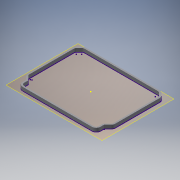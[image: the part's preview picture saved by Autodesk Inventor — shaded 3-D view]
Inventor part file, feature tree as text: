
AUTODESK INVENTOR PART (.ipt)
format: ipt  version: 2017 SP1 (Build 210196100, 196)  size: 916,992 bytes
history: native  units: mm
features: sketch x10, extrude x10, projected_geometry x7, fillet x4, reference x4, other x4, plane x3, shell x1
ambient origin geometry x8: Origin, YZ Plane, XZ Plane, XY Plane, X Axis, Y Axis, Z Axis, Center Point
bodies: Body1 (feature_tree)
feature tree (43):
  plane  "Arbeitsebene3"
  sketch  "Skizze2"  dims[d4=0.3mm d5=0.0mm d6=0.5mm d7=5.0mm d8=0.0mm]
  extrude  "Extrusion2"  Depth=0.5mm
  shell  "Wandung1"  Thickness=5.0mm
  sketch  "Skizze5"  dims[d14=5.0mm d15=0.0mm d18=0.5mm d19=0.0mm]
  plane  "Arbeitsebene4"
  extrude  "Extrusion3"  Depth=0.5mm TaperAngle=0.0deg
  extrude  "Extrusion4"  Depth=2.0mm
  extrude  "Extrusion6"  Depth=30.0mm
  extrude  "Extrusion7"  Depth=3.0mm
  fillet  "Rundung1"  Radius=3.0mm
  extrude  "Extrusion8"  Depth=2.0mm TaperAngle=0.0deg
  fillet  "Rundung2"  Radius=1.0mm
  extrude  "Extrusion9"  Depth=10.0mm
  fillet  "Rundung3"  Radius=3.0mm
  plane  "Arbeitsebene5"
  extrude  "Extrusion10"  Depth=1.0mm
  extrude  "Extrusion11"  Depth=11.0mm
  fillet  "Rundung4"  Radius=11.0mm
  extrude  "Extrusion12"  Depth=0.1mm
  reference  "Referenz1"
  sketch  "Skizze6"  dims[d20=3.0mm d21=0.0mm d22=2.0mm]
  projected_geometry  "Projizierte Kontur3"
  sketch  "Skizze8"  dims[d23=30.0mm d24=30.0mm]
  projected_geometry  "Projizierte Kontur5"
  sketch  "Skizze9"  dims[d25=3.0mm d26=3.0mm d27=3.0mm]
  projected_geometry  "Projizierte Kontur6"
  sketch  "Skizze11"  dims[d28=3.0mm d29=2.0mm d30=0.0mm d31=1.0mm]
  projected_geometry  "Projizierte Kontur7"
  sketch  "Skizze12"  dims[d32=5.0mm d33=10.0mm d34=3.0mm]
  projected_geometry  "Projizierte Kontur8"
  projected_geometry  "Projizierte Kontur9"
  sketch  "Skizze14"  dims[d35=2.0mm d36=0.0mm d37=1.0mm]
  reference  "Referenz5"
  reference  "Referenz6"
  reference  "Referenz7"
  projected_geometry  "Projizierte Kontur10"
  sketch  "Skizze15"  dims[d38=11.0mm d39=11.0mm d40=11.0mm]
  sketch  "Skizze17"  dims[d41=2.0mm d42=0.0mm d43=6.0mm d44=6.0mm d45=6.0mm d46=3.5mm d47=0.0mm d48=1.0mm d49=0.1mm d50=0.0mm]
  other  "<userpath>\Dropbox\Elektronik\aXe_Dashboard240XL\Gehäuse\Montiert.iam"
  other  "Montiert.iam"
  other  "GehäuseDeckel:1"
  other  "PCB_SingleLedRow:1"
